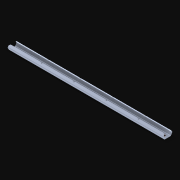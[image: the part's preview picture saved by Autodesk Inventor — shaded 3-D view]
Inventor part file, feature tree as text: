
AUTODESK INVENTOR PART (.ipt)
format: ipt  version: 2021 (Build 250183000, 183)  size: 473,088 bytes
history: native  units: in
note: dims shown in document units (in); Inventor stores cm internally (conversion verified against a paired STEP export)
features: other x25, extrude x24, imported_body x1, pattern_linear x1
ambient origin geometry x8: Origin, YZ Plane, XZ Plane, XY Plane, X Axis, Y Axis, Z Axis, Center Point
bodies: Body1 (feature_tree), Body2 (feature_tree), Body3 (feature_tree), Body4 (feature_tree), Body5 (feature_tree), Body6 (feature_tree), Body7 (feature_tree), Body8 (feature_tree), Body9 (feature_tree), Body10 (feature_tree), Body11 (feature_tree), Body12 (feature_tree), Body13 (feature_tree), Body14 (feature_tree), Body15 (feature_tree), Body16 (feature_tree), Body17 (feature_tree), Body18 (feature_tree), Body19 (feature_tree), Body20 (feature_tree), Body21 (feature_tree), Body22 (feature_tree), Body23 (feature_tree), Body24 (feature_tree), Body25 (feature_tree)
feature tree (51):
  parser-record x1  (decoder bookkeeping rows leaked as tree rows — omitted from the tree; the rows remain in map.json)
  imported_body  "Base1"
  pattern_linear  "Rectangular Pattern1"  Spacing1=0.046in  [1 undecoded]
  other  "Srf1"
  other  "Srf2"
  other  "Srf3"
  other  "Srf4"
  other  "Srf5"
  other  "Srf6"
  other  "Srf7"
  other  "Srf8"
  other  "Srf9"
  other  "Srf10"
  other  "Srf11"
  other  "Srf12"
  other  "Srf13"
  other  "Srf14"
  other  "Srf15"
  other  "Srf16"
  other  "Srf17"
  other  "Srf18"
  other  "Srf19"
  other  "Srf20"
  other  "Srf21"
  other  "Srf22"
  other  "Srf23"
  other  "Srf24"
  extrude  "ExtrusionSrf1"  Depth=0.5in
  extrude  "ExtrusionSrf2"  [1 undecoded]
  extrude  "ExtrusionSrf3"  [1 undecoded]
  extrude  "ExtrusionSrf4"  [1 undecoded]
  extrude  "ExtrusionSrf5"  [1 undecoded]
  extrude  "ExtrusionSrf6"  [1 undecoded]
  extrude  "ExtrusionSrf7"  [1 undecoded]
  extrude  "ExtrusionSrf8"  [1 undecoded]
  extrude  "ExtrusionSrf9"  [1 undecoded]
  extrude  "ExtrusionSrf10"  [1 undecoded]
  extrude  "ExtrusionSrf11"  [1 undecoded]
  extrude  "ExtrusionSrf12"  [1 undecoded]
  extrude  "ExtrusionSrf13"  [1 undecoded]
  extrude  "ExtrusionSrf14"  [1 undecoded]
  extrude  "ExtrusionSrf15"  [1 undecoded]
  extrude  "ExtrusionSrf16"  [1 undecoded]
  extrude  "ExtrusionSrf17"  [1 undecoded]
  extrude  "ExtrusionSrf18"  [1 undecoded]
  extrude  "ExtrusionSrf19"  [1 undecoded]
  extrude  "ExtrusionSrf20"  [1 undecoded]
  extrude  "ExtrusionSrf21"  [1 undecoded]
  extrude  "ExtrusionSrf22"  [1 undecoded]
  extrude  "ExtrusionSrf23"  [1 undecoded]
  extrude  "ExtrusionSrf24"  [1 undecoded]
note: 24 required parameter values undecoded (feature->parameter linkage not recoverable at this tier; creation-order binding heuristic only, values carry confidence <= 0.55)
